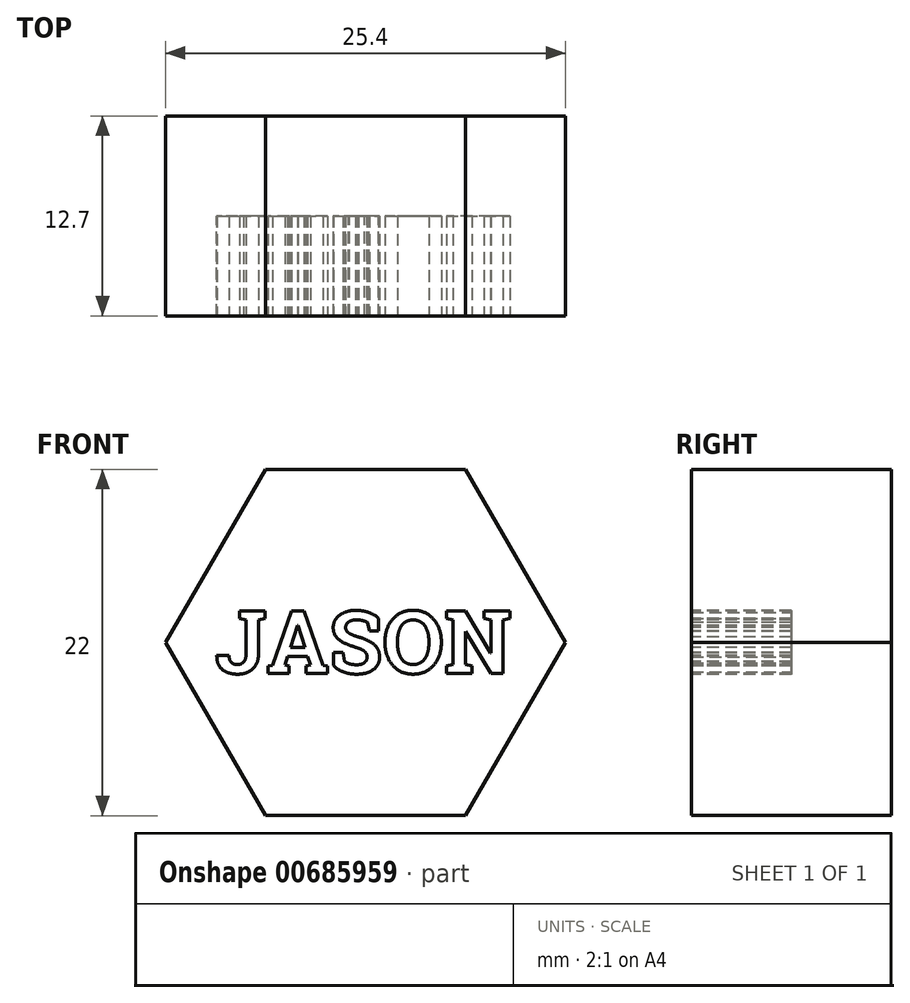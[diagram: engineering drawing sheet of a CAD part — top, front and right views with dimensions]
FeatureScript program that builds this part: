
annotation { "Feature Type Name" : "Feature", "Feature Type Description" : "" }
export const myFeature = defineFeature(function(context is Context, id is Id, definition is map)
    precondition{}
    {
        {
            var Q0;
            Q0=qCreatedBy(makeId("Front.planeOp"),FACE);
            var sketch = newSketch(context, id + "F0", { "sketchPlane" : qUnion([Q0])});
            skCircle(sketch, "E0.cCircle", {"center": v(0, 0) * mm, "radius": 12.7 * mm, "construction": true});
            skLineSegment(sketch, "E0.0", {"start": v(12.7, 0) * mm, "end": v(6.35, -11) * mm});
            skLineSegment(sketch, "E0.1", {"start": v(6.35, -11) * mm, "end": v(-6.35, -11) * mm});
            skLineSegment(sketch, "E0.2", {"start": v(-6.35, -11) * mm, "end": v(-12.7, 0) * mm});
            skLineSegment(sketch, "E0.3", {"start": v(-12.7, 0) * mm, "end": v(-6.35, 11) * mm});
            skLineSegment(sketch, "E0.4", {"start": v(-6.35, 11) * mm, "end": v(6.35, 11) * mm});
            skLineSegment(sketch, "E0.5", {"start": v(6.35, 11) * mm, "end": v(12.7, 0) * mm});
            skSolve(sketch);
        }
        {
            var Q0;
            Q0=makeQuery(id+"F0.imprint","IMPRINT",FACE,{"disambiguationData":[TD([[makeQuery(id+"F0.imprint","IMPRINT",EDGE,{"derivedFrom":sQuery(id+"F0.wireOp",EDGE,"E0.0")}),-1.0]])]});
            extrude(context, id + "F1", {"entities" : qUnion([Q0]), "depth" : 12.7 * mm, "offsetDistance" : 25.4 * mm});
        }
        {
            var Q0;
            Q0=makeQuery(id+"F1.opExtrude","CAP_FACE",FACE,{"disambiguationData":[OSD([sQuery(id+"F0.wireOp",EDGE,"E0.0"),sQuery(id+"F0.wireOp",EDGE,"E0.1"),sQuery(id+"F0.wireOp",EDGE,"E0.2"),sQuery(id+"F0.wireOp",EDGE,"E0.3"),sQuery(id+"F0.wireOp",EDGE,"E0.4"),sQuery(id+"F0.wireOp",EDGE,"E0.5")])],"isStart":false});
            var sketch = newSketch(context, id + "F2", { "sketchPlane" : qUnion([Q0])});
            skText(sketch, "E1", { "text": "JASON", "fontName": "RobotoSlab-Bold.ttf"});
            const initialGuessF2  = {"E1": [-0.00954, -0.00196, 1, 0, 0.004]};
            skSetInitialGuess(sketch, initialGuessF2);
            skSolve(sketch);
        }
        {
            var Q0;
            Q0 = qSketchRegion(id + "F2", true);
            extrude(context, id + "F3", {"entities" : qUnion([Q0]), "operationType" : NewBodyOperationType.REMOVE, "oppositeDirection" : true, "depth" : 6.35 * mm, "offsetDistance" : 25.4 * mm});
        }
    });
